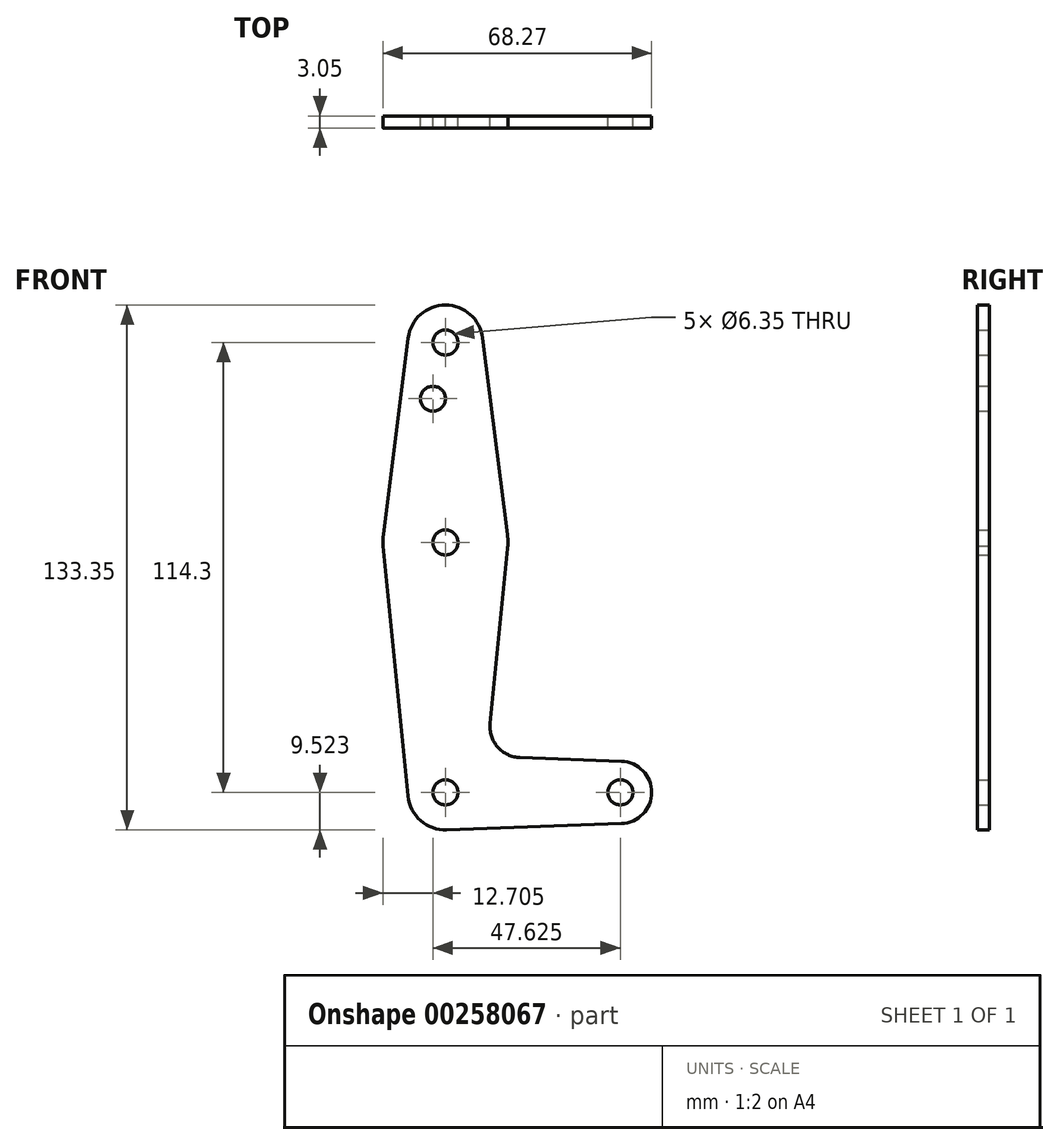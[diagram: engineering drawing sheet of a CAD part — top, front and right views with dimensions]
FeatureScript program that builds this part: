
annotation { "Feature Type Name" : "Feature", "Feature Type Description" : "" }
export const myFeature = defineFeature(function(context is Context, id is Id, definition is map)
    precondition{}
    {
        {
            var Q0;
            Q0=qCreatedBy(makeId("Front.planeOp"),FACE);
            var sketch = newSketch(context, id + "F0", { "sketchPlane" : qUnion([Q0])});
            skCircle(sketch, "E0", {"center": v(0, 63.43) * mm, "radius": 9.53 * mm});
            skCircle(sketch, "E1", {"center": v(0, 12.63) * mm, "radius": 15.88 * mm});
            skCircle(sketch, "E2", {"center": v(0, -50.87) * mm, "radius": 9.53 * mm});
            skCircle(sketch, "E3", {"center": v(44.45, -50.87) * mm, "radius": 7.94 * mm});
            skLineSegment(sketch, "E4", {"start": v(-9.45, 64.62) * mm, "end": v(-15.75, 14.62) * mm});
            skLineSegment(sketch, "E5", {"start": v(9.45, 64.62) * mm, "end": v(15.85, 13.8) * mm});
            skLineSegment(sketch, "E6", {"start": v(-15.85, 11.75) * mm, "end": v(-9.48, -51.82) * mm});
            skCircle(sketch, "E7", {"center": v(0, 63.43) * mm, "radius": 3.18 * mm});
            skCircle(sketch, "E8", {"center": v(0, 12.63) * mm, "radius": 3.18 * mm});
            skCircle(sketch, "E9", {"center": v(-3.18, 49.16) * mm, "radius": 3.18 * mm});
            skCircle(sketch, "E10", {"center": v(0, -50.87) * mm, "radius": 3.18 * mm});
            skCircle(sketch, "E11", {"center": v(44.45, -50.87) * mm, "radius": 3.18 * mm});
            skPoint(sketch, "E12.newPointA", {"position": v(0, -41.34) * mm});
            skLineSegment(sketch, "E13", {"start": v(0.34, -60.39) * mm, "end": v(44.73, -58.8) * mm});
            skLineSegment(sketch, "E14", {"start": v(15.8, 11.05) * mm, "end": v(11.35, -33.3) * mm});
            skLineSegment(sketch, "E15", {"start": v(18.98, -42.03) * mm, "end": v(44.73, -42.93) * mm});
            skArc(sketch, "E16.filletArc", {"start": v(11.35, -33.3) * mm, "mid": v(13.27, -39.32) * mm, "end": v(18.98, -42.03) * mm});
            skSolve(sketch);
        }
        {
            var Q0;
            {var subQ5=sQuery(id+"F0.wireOp",EDGE,"E4");Q0=makeQuery(id+"F0.imprint","IMPRINT",FACE,{"disambiguationData":[TD([[makeQuery(id+"F0.imprint","IMPRINT",EDGE,{"derivedFrom":subQ5}),1.0]])]});}
            var Q1;
            Q1=makeQuery(id+"F0.imprint","IMPRINT",FACE,{"disambiguationData":[TD([[makeQuery(id+"F0.imprint","IMPRINT",EDGE,{"derivedFrom":sQuery(id+"F0.wireOp",EDGE,"E7")}),-1.0]])]});
            var Q2;
            Q2=makeQuery(id+"F0.imprint","IMPRINT",FACE,{"disambiguationData":[TD([[makeQuery(id+"F0.imprint","IMPRINT",EDGE,{"derivedFrom":sQuery(id+"F0.wireOp",EDGE,"E8")}),-1.0]])]});
            var Q3;
            {var subQ5=sQuery(id+"F0.wireOp",EDGE,"WZwPLZDt-7eUM-Yfsk-SdDR-WqWhp6LwKX20");Q3=makeQuery(id+"F0.imprint","IMPRINT",FACE,{"disambiguationData":[TD([[makeQuery(id+"F0.imprint","IMPRINT",EDGE,{"derivedFrom":subQ5}),1.0]])]});}
            var Q4;
            Q4=makeQuery(id+"F0.imprint","IMPRINT",FACE,{"disambiguationData":[TD([[makeQuery(id+"F0.imprint","IMPRINT",EDGE,{"derivedFrom":sQuery(id+"F0.wireOp",EDGE,"E10")}),-1.0]])]});
            var Q5;
            Q5=makeQuery(id+"F0.imprint","IMPRINT",FACE,{"disambiguationData":[TD([[makeQuery(id+"F0.imprint","IMPRINT",EDGE,{"derivedFrom":sQuery(id+"F0.wireOp",EDGE,"E11")}),-1.0]])]});
            var Q6;
            {var subQ5=sQuery(id+"F0.wireOp",EDGE,"E13");Q6=makeQuery(id+"F0.imprint","IMPRINT",FACE,{"disambiguationData":[TD([[makeQuery(id+"F0.imprint","IMPRINT",EDGE,{"derivedFrom":subQ5}),1.0]])]});}
            extrude(context, id + "F1", {"entities" : qUnion([Q0, Q1, Q2, Q3, Q4, Q5, Q6]), "depth" : 3.05 * mm});
        }
    });
